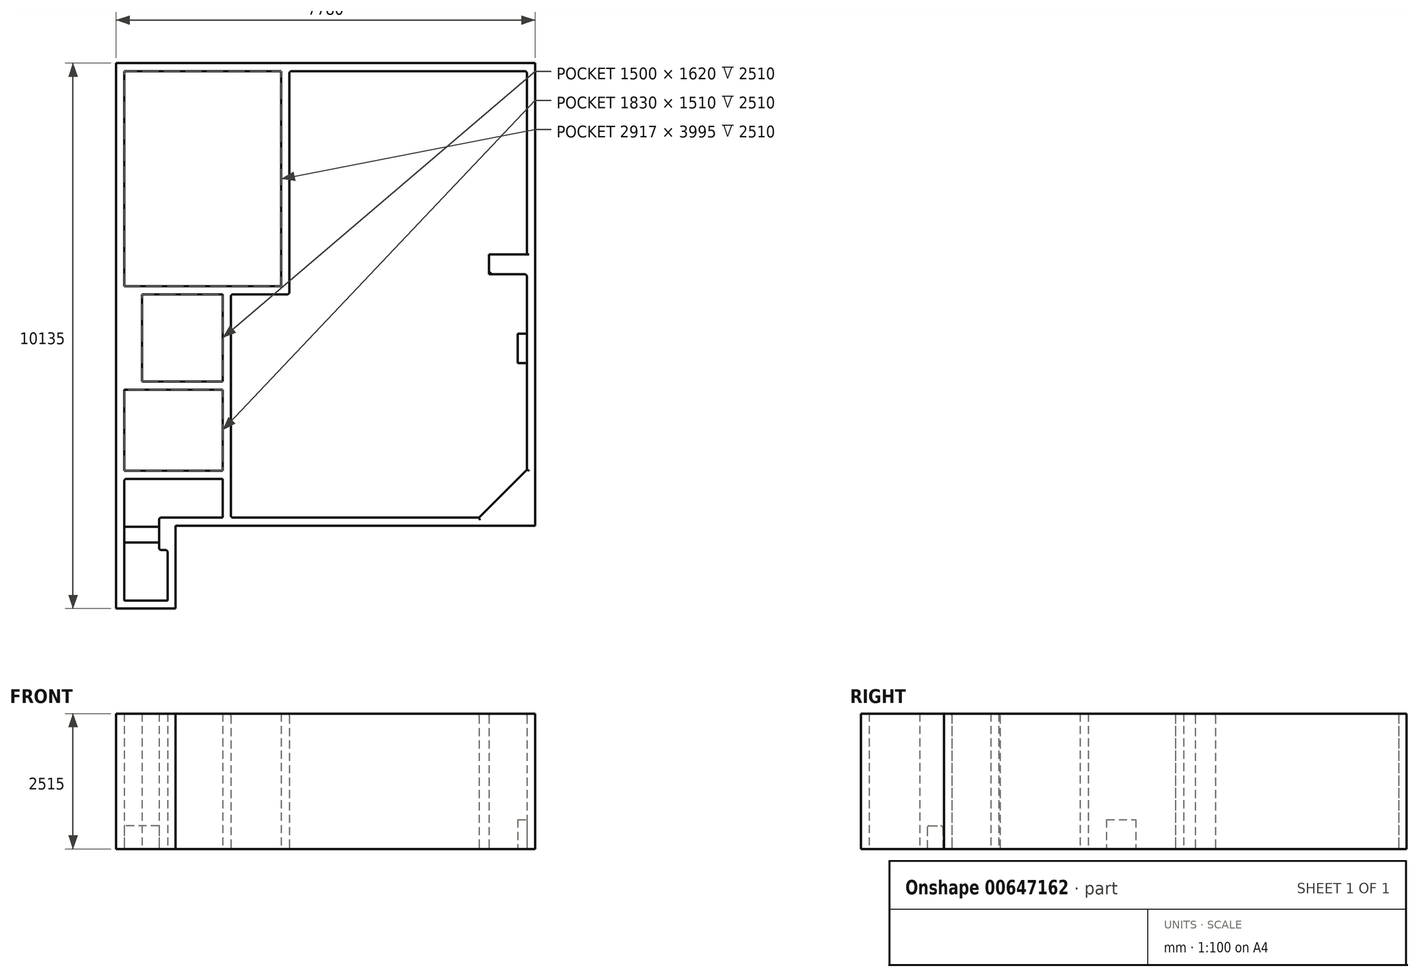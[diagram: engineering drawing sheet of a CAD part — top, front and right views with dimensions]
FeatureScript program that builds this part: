
annotation { "Feature Type Name" : "Feature", "Feature Type Description" : "" }
export const myFeature = defineFeature(function(context is Context, id is Id, definition is map)
    precondition{}
    {
        {
            var Q0;
            Q0=qCreatedBy(makeId("Top.planeOp"),FACE);
            var sketch = newSketch(context, id + "F0", { "sketchPlane" : qUnion([Q0])});
            skLineSegment(sketch, "E0.top", {"start": v(-2210, -5120) * mm, "end": v(-1105, -5120) * mm});
            skLineSegment(sketch, "E0.left", {"start": v(-2210, -2560) * mm, "end": v(-2210, -5120) * mm});
            skLineSegment(sketch, "E0.right", {"start": v(-1105, -3580) * mm, "end": v(-1105, -5120) * mm});
            skLineSegment(sketch, "E1", {"start": v(-1105, -4030) * mm, "end": v(-1415, -4030) * mm});
            skLineSegment(sketch, "E2", {"start": v(-1415, -4030) * mm, "end": v(-1415, -3580) * mm});
            skLineSegment(sketch, "E3", {"start": v(0, 1488.12) * mm, "end": v(0, -1442.93) * mm, "construction": true});
            skLineSegment(sketch, "E4", {"start": v(-1334.23, 0) * mm, "end": v(968.74, 0) * mm, "construction": true});
            skLineSegment(sketch, "E5", {"start": v(-230, -2560) * mm, "end": v(-230, -3580) * mm});
            skLineSegment(sketch, "E6", {"start": v(-2060, -2560) * mm, "end": v(-230, -2560) * mm});
            skLineSegment(sketch, "E7", {"start": v(-1105, -3580) * mm, "end": v(-230, -3580) * mm});
            skLineSegment(sketch, "E8.bottom", {"start": v(-230, -3580) * mm, "end": v(5570, -3580) * mm});
            skLineSegment(sketch, "E8.top", {"start": v(857, 5015) * mm, "end": v(5570, 5015) * mm});
            skLineSegment(sketch, "E8.left", {"start": v(-230, -3580) * mm, "end": v(-230, 720) * mm});
            skLineSegment(sketch, "E8.right", {"start": v(5570, -3580) * mm, "end": v(5570, 5015) * mm});
            skLineSegment(sketch, "E9", {"start": v(-230, -900) * mm, "end": v(-2210, -900) * mm});
            skLineSegment(sketch, "E10", {"start": v(-2210, -900) * mm, "end": v(-2210, -2560) * mm});
            skLineSegment(sketch, "E11", {"start": v(-230, 870) * mm, "end": v(-1880, 870) * mm});
            skLineSegment(sketch, "E12", {"start": v(-1880, 570) * mm, "end": v(-1880, -750) * mm});
            skLineSegment(sketch, "E13", {"start": v(857, 870) * mm, "end": v(857, 4865) * mm});
            skLineSegment(sketch, "E14", {"start": v(-230, 870) * mm, "end": v(857, 870) * mm});
            skLineSegment(sketch, "E15", {"start": v(-2210, -900) * mm, "end": v(-2210, 5015) * mm});
            skLineSegment(sketch, "E16", {"start": v(857, 5015) * mm, "end": v(-2210, 5015) * mm});
            skLineSegment(sketch, "E17.0", {"start": v(1007, 720) * mm, "end": v(1007, 4865) * mm});
            skLineSegment(sketch, "E17.1", {"start": v(5420, -3430) * mm, "end": v(5420, 4865) * mm});
            skLineSegment(sketch, "E17.2", {"start": v(-80, -3430) * mm, "end": v(5420, -3430) * mm});
            skLineSegment(sketch, "E17.3", {"start": v(1007, 4865) * mm, "end": v(5420, 4865) * mm});
            skLineSegment(sketch, "E17.4", {"start": v(-80, -3430) * mm, "end": v(-80, 720) * mm});
            skLineSegment(sketch, "E17.5", {"start": v(-80, 720) * mm, "end": v(1007, 720) * mm});
            skLineSegment(sketch, "E18.0", {"start": v(-2060, -2710) * mm, "end": v(-230, -2710) * mm});
            skLineSegment(sketch, "E18.1", {"start": v(-2060, -2710) * mm, "end": v(-2060, -4970) * mm});
            skLineSegment(sketch, "E18.2", {"start": v(-2060, -4970) * mm, "end": v(-1255, -4970) * mm});
            skLineSegment(sketch, "E19.0", {"start": v(-1255, -4030) * mm, "end": v(-1255, -4970) * mm});
            skLineSegment(sketch, "E20.0", {"start": v(-1415, -3430) * mm, "end": v(-230, -3430) * mm});
            skLineSegment(sketch, "E21", {"start": v(-1415, -3580) * mm, "end": v(-1415, -3430) * mm});
            skLineSegment(sketch, "E22.0", {"start": v(-2060, -1050) * mm, "end": v(-2060, -2560) * mm});
            skLineSegment(sketch, "E22.1", {"start": v(-230, -1050) * mm, "end": v(-2060, -1050) * mm});
            skLineSegment(sketch, "E23", {"start": v(-1880, 870) * mm, "end": v(-2210, 870) * mm});
            skLineSegment(sketch, "E24.0", {"start": v(-1730, 720) * mm, "end": v(-1730, -900) * mm});
            skLineSegment(sketch, "E24.1", {"start": v(-230, 720) * mm, "end": v(-1730, 720) * mm});
            skLineSegment(sketch, "E25.0", {"start": v(-2060, 870) * mm, "end": v(-2060, 4865) * mm});
            skLineSegment(sketch, "E25.1", {"start": v(857, 4865) * mm, "end": v(-2060, 4865) * mm});
            skLineSegment(sketch, "E26.0", {"start": v(-1880, 570) * mm, "end": v(-2210, 570) * mm});
            skLineSegment(sketch, "E27.0", {"start": v(-1880, -750) * mm, "end": v(-2210, -750) * mm});
            skLineSegment(sketch, "E28", {"start": v(5420, -2539.05) * mm, "end": v(4529.05, -3430) * mm});
            skLineSegment(sketch, "E29", {"start": v(5420, 1090.95) * mm, "end": v(4715, 1090.95) * mm});
            skLineSegment(sketch, "E30", {"start": v(4715, 1090.95) * mm, "end": v(4715, 1460.95) * mm});
            skLineSegment(sketch, "E31", {"start": v(4715, 1460.95) * mm, "end": v(5420, 1460.95) * mm});
            skLineSegment(sketch, "E32", {"start": v(-1415, -3600) * mm, "end": v(-2060, -3600) * mm});
            skLineSegment(sketch, "E33", {"start": v(-1415, -3890) * mm, "end": v(-2060, -3890) * mm});
            skLineSegment(sketch, "E34", {"start": v(5420, -14.05) * mm, "end": v(5250, -14.05) * mm});
            skLineSegment(sketch, "E35", {"start": v(5250, -14.05) * mm, "end": v(5250, -559.05) * mm});
            skLineSegment(sketch, "E36", {"start": v(5250, -559.05) * mm, "end": v(5420, -559.05) * mm});
            skSolve(sketch);
        }
        {
            var Q0;
            Q0=qSketchRegion(id+"F0",true);
            extrude(context, id + "F1", {"entities" : qUnion([Q0]), "depth" : 2510 * mm, "offsetDistance" : 25.4 * mm});
        }
        {
            var Q0;
            {var subQ3=sQuery(id+"F0.wireOp",EDGE,"E28");Q0=makeQuery(id+"F0.imprint","IMPRINT",FACE,{"disambiguationData":[TD([[makeQuery(id+"F0.imprint","IMPRINT",EDGE,{"derivedFrom":subQ3}),1.0]])]});}
            extrude(context, id + "F2", {"entities" : qUnion([Q0]), "operationType" : NewBodyOperationType.ADD, "depth" : 2510 * mm, "offsetDistance" : 25.4 * mm});
        }
        {
            var Q0;
            {var subQ0=sQuery(id+"F0.wireOp",EDGE,"E29");Q0=makeQuery(id+"F0.imprint","IMPRINT",FACE,{"disambiguationData":[TD([[makeQuery(id+"F0.imprint","IMPRINT",EDGE,{"derivedFrom":subQ0}),-1.0]])]});}
            extrude(context, id + "F3", {"entities" : qUnion([Q0]), "operationType" : NewBodyOperationType.ADD, "depth" : 2510 * mm, "offsetDistance" : 25.4 * mm});
        }
        {
            var Q0;
            {var subQ0=sQuery(id+"F0.wireOp",EDGE,"E32");Q0=makeQuery(id+"F0.imprint","IMPRINT",FACE,{"disambiguationData":[TD([[makeQuery(id+"F0.imprint","IMPRINT",EDGE,{"derivedFrom":subQ0}),1.0]])]});}
            extrude(context, id + "F4", {"entities" : qUnion([Q0]), "operationType" : NewBodyOperationType.ADD, "depth" : 425 * mm, "offsetDistance" : 25.4 * mm});
        }
        {
            var Q0;
            Q0=makeQuery(id+"F1.opExtrude","SWEPT_EDGE",EDGE,{"disambiguationData":[OSD([sQuery(id+"F0.wireOp",EDGE,"E1"),sQuery(id+"F0.wireOp",EDGE,"E19.0")])]});
            var Q1;
            Q1=makeQuery(id+"F1.opExtrude","SWEPT_EDGE",EDGE,{"disambiguationData":[OSD([sQuery(id+"F0.wireOp",EDGE,"E1"),sQuery(id+"F0.wireOp",EDGE,"E2")])]});
            var Q2;
            Q2=makeQuery(id+"F1.opExtrude","SWEPT_EDGE",EDGE,{"disambiguationData":[OSD([sQuery(id+"F0.wireOp",EDGE,"E20.0"),sQuery(id+"F0.wireOp",EDGE,"E21")])]});
            var Q3;
            Q3=makeQuery(id+"F4.opExtrude","CAP_EDGE",EDGE,{"disambiguationData":[OSD([sQuery(id+"F0.wireOp",EDGE,"E33")])],"isStart":false});
            var Q4;
            Q4=makeQuery(id+"F4.opExtrude","CAP_EDGE",EDGE,{"disambiguationData":[OSD([sQuery(id+"F0.wireOp",EDGE,"E32")])],"isStart":false});
            var Q5;
            Q5=makeQuery(id+"F3.opExtrude","SWEPT_EDGE",EDGE,{"disambiguationData":[OSD([sQuery(id+"F0.wireOp",EDGE,"E17.1"),sQuery(id+"F0.wireOp",EDGE,"E29")])]});
            var Q6;
            Q6=makeQuery(id+"F3.opExtrude","SWEPT_EDGE",EDGE,{"disambiguationData":[OSD([sQuery(id+"F0.wireOp",EDGE,"E17.1"),sQuery(id+"F0.wireOp",EDGE,"E31")])]});
            var Q7;
            Q7=makeQuery(id+"F1.opExtrude","SWEPT_EDGE",EDGE,{"disambiguationData":[OSD([sQuery(id+"F0.wireOp",EDGE,"E17.1"),sQuery(id+"F0.wireOp",EDGE,"E17.3")])]});
            var Q8;
            Q8=makeQuery(id+"F1.opExtrude","SWEPT_EDGE",EDGE,{"disambiguationData":[OSD([sQuery(id+"F0.wireOp",EDGE,"E17.0"),sQuery(id+"F0.wireOp",EDGE,"E17.3")])]});
            var Q9;
            Q9=makeQuery(id+"F1.opExtrude","SWEPT_EDGE",EDGE,{"disambiguationData":[OSD([sQuery(id+"F0.wireOp",EDGE,"E17.0"),sQuery(id+"F0.wireOp",EDGE,"E17.5")])]});
            var Q10;
            Q10=makeQuery(id+"F1.opExtrude","SWEPT_EDGE",EDGE,{"disambiguationData":[OSD([sQuery(id+"F0.wireOp",EDGE,"E17.4"),sQuery(id+"F0.wireOp",EDGE,"E17.5")])]});
            var Q11;
            Q11=makeQuery(id+"F1.opExtrude","SWEPT_EDGE",EDGE,{"disambiguationData":[OSD([sQuery(id+"F0.wireOp",EDGE,"E18.0"),sQuery(id+"F0.wireOp",EDGE,"E18.1")])]});
            fillet(context, id + "F5", {"entities" : qUnion([Q0, Q1, Q2, Q3, Q4, Q5, Q6, Q7, Q8, Q9, Q10, Q11]), "radius" : 40 * mm, "tangentPropagation" : true, "allowEdgeOverflow" : false});
        }
        {
            var Q0;
            {var subQ0=sQuery(id+"F0.wireOp",EDGE,"E18.1");var subQ1=sQuery(id+"F0.wireOp",EDGE,"E2");var subQ2=sQuery(id+"F0.wireOp",EDGE,"E17.1");var subQ3=sQuery(id+"F0.wireOp",EDGE,"E17.2");Q0=makeQuery(id+"F4.boolean.opBoolean","MERGE",FACE,{"derivedFrom":[makeQuery(id+"F3.boolean.opBoolean","MERGE",FACE,{"derivedFrom":[makeQuery(id+"F2.boolean.opBoolean","MERGE",FACE,{"derivedFrom":[makeQuery(id+"F1.opExtrude","CAP_FACE",FACE,{"disambiguationData":[OSD([sQuery(id+"F0.wireOp",EDGE,"E0.top"),sQuery(id+"F0.wireOp",EDGE,"E0.left"),sQuery(id+"F0.wireOp",EDGE,"E0.right"),sQuery(id+"F0.wireOp",EDGE,"E1"),subQ1,sQuery(id+"F0.wireOp",EDGE,"E6"),sQuery(id+"F0.wireOp",EDGE,"E7"),sQuery(id+"F0.wireOp",EDGE,"E8.bottom"),sQuery(id+"F0.wireOp",EDGE,"E8.top"),sQuery(id+"F0.wireOp",EDGE,"E8.left"),sQuery(id+"F0.wireOp",EDGE,"E8.right"),sQuery(id+"F0.wireOp",EDGE,"E9"),sQuery(id+"F0.wireOp",EDGE,"E10"),sQuery(id+"F0.wireOp",EDGE,"E11"),sQuery(id+"F0.wireOp",EDGE,"E13"),sQuery(id+"F0.wireOp",EDGE,"E14"),sQuery(id+"F0.wireOp",EDGE,"E15"),sQuery(id+"F0.wireOp",EDGE,"E16"),sQuery(id+"F0.wireOp",EDGE,"E17.0"),subQ2,subQ3,sQuery(id+"F0.wireOp",EDGE,"E17.3"),sQuery(id+"F0.wireOp",EDGE,"E17.4"),sQuery(id+"F0.wireOp",EDGE,"E17.5"),sQuery(id+"F0.wireOp",EDGE,"E18.0"),subQ0,sQuery(id+"F0.wireOp",EDGE,"E18.2"),sQuery(id+"F0.wireOp",EDGE,"E19.0"),sQuery(id+"F0.wireOp",EDGE,"E20.0"),sQuery(id+"F0.wireOp",EDGE,"E21"),sQuery(id+"F0.wireOp",EDGE,"E22.0"),sQuery(id+"F0.wireOp",EDGE,"E22.1"),sQuery(id+"F0.wireOp",EDGE,"E23"),sQuery(id+"F0.wireOp",EDGE,"E24.0"),sQuery(id+"F0.wireOp",EDGE,"E24.1"),sQuery(id+"F0.wireOp",EDGE,"E25.0"),sQuery(id+"F0.wireOp",EDGE,"E25.1")])],"isStart":true}),makeQuery(id+"F2.opExtrude","CAP_FACE",FACE,{"disambiguationData":[OSD([subQ2,subQ3,sQuery(id+"F0.wireOp",EDGE,"E28")])],"isStart":true})]}),makeQuery(id+"F3.opExtrude","CAP_FACE",FACE,{"disambiguationData":[OSD([subQ2,sQuery(id+"F0.wireOp",EDGE,"E29"),sQuery(id+"F0.wireOp",EDGE,"E30"),sQuery(id+"F0.wireOp",EDGE,"E31")])],"isStart":true})]}),makeQuery(id+"F4.opExtrude","CAP_FACE",FACE,{"disambiguationData":[OSD([subQ1,subQ0,sQuery(id+"F0.wireOp",EDGE,"E32"),sQuery(id+"F0.wireOp",EDGE,"E33")])],"isStart":true})]});}
            var sketch = newSketch(context, id + "F6", { "sketchPlane" : qUnion([Q0])});
            skLineSegment(sketch, "E37.bottom", {"start": v(-2210, -5015) * mm, "end": v(5570, -5015) * mm});
            skLineSegment(sketch, "E37.top", {"start": v(-2210, 3580) * mm, "end": v(5570, 3580) * mm});
            skLineSegment(sketch, "E37.left", {"start": v(-2210, -5015) * mm, "end": v(-2210, 3580) * mm});
            skLineSegment(sketch, "E37.right", {"start": v(5570, -5015) * mm, "end": v(5570, 3580) * mm});
            skLineSegment(sketch, "E38.bottom", {"start": v(-2210, 3580) * mm, "end": v(-1105, 3580) * mm});
            skLineSegment(sketch, "E38.top", {"start": v(-2210, 5120) * mm, "end": v(-1105, 5120) * mm});
            skLineSegment(sketch, "E38.left", {"start": v(-2210, 3580) * mm, "end": v(-2210, 5120) * mm});
            skLineSegment(sketch, "E38.right", {"start": v(-1105, 3580) * mm, "end": v(-1105, 5120) * mm});
            skSolve(sketch);
        }
        {
            var Q0;
            Q0=qSketchRegion(id+"F6",true);
            extrude(context, id + "F7", {"entities" : qUnion([Q0]), "operationType" : NewBodyOperationType.ADD, "depth" : 5 * mm, "offsetDistance" : 25.4 * mm});
        }
        {
            var Q0;
            Q0=makeQuery(id+"F1.opExtrude","CAP_EDGE",EDGE,{"disambiguationData":[OSD([sQuery(id+"F0.wireOp",EDGE,"E17.4")])],"isStart":false});
            var Q1;
            Q1=makeQuery(id+"F1.opExtrude","CAP_EDGE",EDGE,{"disambiguationData":[OSD([sQuery(id+"F0.wireOp",EDGE,"E17.5")])],"isStart":false});
            var Q2;
            Q2=makeQuery(id+"F1.opExtrude","CAP_EDGE",EDGE,{"disambiguationData":[OSD([sQuery(id+"F0.wireOp",EDGE,"E17.0")])],"isStart":false});
            var Q3;
            Q3=makeQuery(id+"F1.opExtrude","CAP_EDGE",EDGE,{"disambiguationData":[OSD([sQuery(id+"F0.wireOp",EDGE,"E17.3")])],"isStart":false});
            var Q4;
            {var subQ0=sQuery(id+"F0.wireOp",EDGE,"E17.3");var subQ2=sQuery(id+"F0.wireOp",EDGE,"E17.1");Q4=makeQuery(id+"F3.boolean.opBoolean","SPLIT",EDGE,{"disambiguationData":[TD([makeQuery(id+"F1.opExtrude","SWEPT_FACE",FACE,{"disambiguationData":[OSD([subQ0])]})])],"derivedFrom":makeQuery(id+"F1.opExtrude","CAP_EDGE",EDGE,{"disambiguationData":[OSD([subQ2])],"isStart":false})});}
            var Q5;
            {var subQ0=sQuery(id+"F0.wireOp",EDGE,"E28");var subQ2=sQuery(id+"F0.wireOp",EDGE,"E17.1");Q5=makeQuery(id+"F3.boolean.opBoolean","SPLIT",EDGE,{"disambiguationData":[TD([makeQuery(id+"F2.opExtrude","SWEPT_FACE",FACE,{"disambiguationData":[OSD([subQ0])]})])],"derivedFrom":makeQuery(id+"F1.opExtrude","CAP_EDGE",EDGE,{"disambiguationData":[OSD([subQ2])],"isStart":false})});}
            var Q6;
            Q6=makeQuery(id+"F2.opExtrude","CAP_EDGE",EDGE,{"disambiguationData":[OSD([sQuery(id+"F0.wireOp",EDGE,"E28")])],"isStart":false});
            var Q7;
            Q7=makeQuery(id+"F1.opExtrude","CAP_EDGE",EDGE,{"disambiguationData":[OSD([sQuery(id+"F0.wireOp",EDGE,"E17.2")])],"isStart":false});
            var Q8;
            Q8=makeQuery(id+"F3.opExtrude","CAP_EDGE",EDGE,{"disambiguationData":[OSD([sQuery(id+"F0.wireOp",EDGE,"E30")])],"isStart":false});
            var Q9;
            Q9=makeQuery(id+"F1.opExtrude","SWEPT_EDGE",EDGE,{"disambiguationData":[OSD([sQuery(id+"F0.wireOp",EDGE,"E17.2"),sQuery(id+"F0.wireOp",EDGE,"E17.4")])]});
            fillet(context, id + "F8", {"entities" : qUnion([Q0, Q1, Q2, Q3, Q4, Q5, Q6, Q7, Q8, Q9]), "radius" : 40 * mm, "tangentPropagation" : true, "allowEdgeOverflow" : false});
        }
        {
            var Q0;
            {var subQ0=sQuery(id+"F0.wireOp",EDGE,"E34");Q0=makeQuery(id+"F0.imprint","IMPRINT",FACE,{"disambiguationData":[TD([[makeQuery(id+"F0.imprint","IMPRINT",EDGE,{"derivedFrom":subQ0}),1.0]])]});}
            extrude(context, id + "F9", {"entities" : qUnion([Q0]), "operationType" : NewBodyOperationType.ADD, "depth" : 540 * mm, "offsetDistance" : 25.4 * mm});
        }
    });
